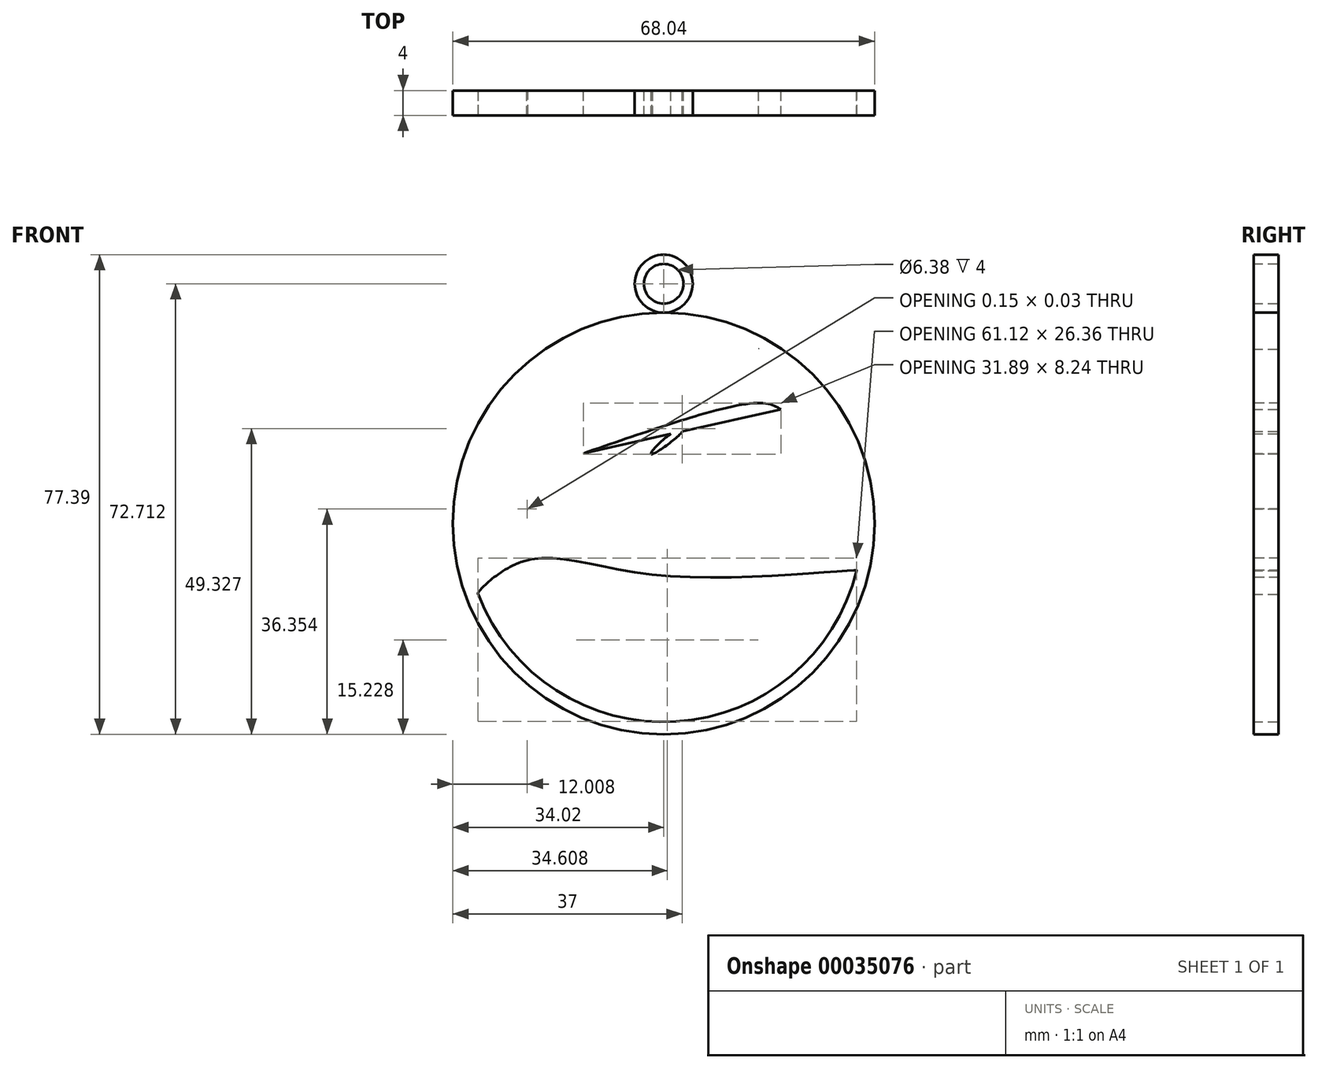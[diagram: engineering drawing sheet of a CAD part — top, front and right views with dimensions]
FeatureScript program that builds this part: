
annotation { "Feature Type Name" : "Feature", "Feature Type Description" : "" }
export const myFeature = defineFeature(function(context is Context, id is Id, definition is map)
    precondition{}
    {
        {
            var Q0;
            Q0=qCreatedBy(makeId("Front.planeOp"),FACE);
            var sketch = newSketch(context, id + "F0", { "sketchPlane" : qUnion([Q0])});
            skCircle(sketch, "E0", {"center": v(0, 0) * mm, "radius": 34.02 * mm});
            skPoint(sketch, "E1", {"position": v(0, 38.7) * mm});
            skCircle(sketch, "E2", {"center": v(0, 38.7) * mm, "radius": 4.67 * mm});
            skCircle(sketch, "E3", {"center": v(0, 38.7) * mm, "radius": 3.19 * mm});
            skCircle(sketch, "E4", {"center": v(0, 0) * mm, "radius": 32.04 * mm});
            skFitSpline(sketch, "E5", {"points": [v(-29.97, -11.33) * mm, v(-24.66, -10.38) * mm, v(22.25, -13.59) * mm, v(31.12, -7.6) * mm, v(31.14, -7.55) * mm, v(0, -8.43) * mm, v(-23.06, -6.25) * mm, v(-29.97, -11.33) * mm]});
            skFitSpline(sketch, "E6", {"points": [v(-23.06, -6.25) * mm, v(-14.23, 0) * mm, v(-29.25, 3.16) * mm, v(-29.02, 3.04) * mm, v(-18.7, 0) * mm], "startDerivative": vector(53.34, 22.76) * mm, "endDerivative": vector(45.6, -13.32) * mm});
            skFitSpline(sketch, "E7", {"points": [v(-18.7, 0) * mm, v(-19.73, -2.8) * mm, v(-23.95, -6.6) * mm, v(-23.06, -6.25) * mm], "startDerivative": vector(-0.5, -7.48) * mm, "endDerivative": vector(7.16, 3.44) * mm});
            skFitSpline(sketch, "E8", {"points": [v(-21.94, 2.33) * mm, v(-24.55, 6.83) * mm, v(-23.06, 6.94) * mm, v(-23.06, 6.83) * mm, v(-21.94, 2.33) * mm]});
            skLineSegment(sketch, "E9", {"start": v(12.5, 12.45) * mm, "end": v(12.5, -4.76) * mm});
            skLineSegment(sketch, "E10", {"start": v(-1.95, 11.19) * mm, "end": v(-1.95, -5.9) * mm});
            skLineSegment(sketch, "E11", {"start": v(-1.95, -5.9) * mm, "end": v(9.52, -6.82) * mm});
            skLineSegment(sketch, "E12", {"start": v(-1.95, 11.19) * mm, "end": v(9.52, 13.25) * mm});
            skLineSegment(sketch, "E13", {"start": v(0, -3.95) * mm, "end": v(0, 8.32) * mm});
            skFitSpline(sketch, "E14", {"points": [v(0, 8.32) * mm, v(1.37, 8.32) * mm, v(9.52, 13.25) * mm], "startDerivative": vector(4.13, -0.94) * mm, "endDerivative": vector(13.5, 9.27) * mm});
            skFitSpline(sketch, "E15", {"points": [v(0, -3.95) * mm, v(1.6, -3.95) * mm, v(9.52, -6.82) * mm], "startDerivative": vector(4.35, 0.63) * mm, "endDerivative": vector(13.49, -5.55) * mm});
            skLineSegment(sketch, "E16", {"start": v(12.5, 12.45) * mm, "end": v(9.52, 13.25) * mm});
            skLineSegment(sketch, "E17", {"start": v(9.52, 13.25) * mm, "end": v(10.13, 9.87) * mm});
            skLineSegment(sketch, "E18", {"start": v(10.13, 9.87) * mm, "end": v(10.13, -4.3) * mm});
            skLineSegment(sketch, "E19", {"start": v(10.13, -4.3) * mm, "end": v(12.5, -4.76) * mm});
            skLineSegment(sketch, "E20", {"start": v(10.13, 5.22) * mm, "end": v(2.3, 4.3) * mm});
            skLineSegment(sketch, "E21", {"start": v(10.13, 0) * mm, "end": v(2.3, -0.92) * mm});
            skFitSpline(sketch, "E22", {"points": [v(2.3, -0.92) * mm, v(3.2, -2.23) * mm, v(10.13, -0.92) * mm], "startDerivative": vector(1.65, -5.05) * mm, "endDerivative": vector(12.72, 3.98) * mm});
            skFitSpline(sketch, "E23", {"points": [v(2.3, 4.3) * mm, v(3.55, 6.14) * mm, v(10.13, 5.22) * mm], "startDerivative": vector(2.17, 6.19) * mm, "endDerivative": vector(12.58, -3.5) * mm});
            skLineSegment(sketch, "E24", {"start": v(-12.96, 11.3) * mm, "end": v(18.92, 18.41) * mm});
            skFitSpline(sketch, "E25", {"points": [v(18.92, 18.41) * mm, v(15.37, 19.45) * mm, v(-12.96, 11.3) * mm], "startDerivative": vector(-10.35, 5.9) * mm, "endDerivative": vector(-47.52, -16.56) * mm});
            skFitSpline(sketch, "E26", {"points": [v(5.73, 17.5) * mm, v(15.3, 28.14) * mm, v(15.3, 28.15) * mm], "startDerivative": vector(14.6, 16.1) * mm, "endDerivative": vector(-0.3, 0.02) * mm});
            skFitSpline(sketch, "E27", {"points": [v(15.3, 28.14) * mm, v(11, 27.02) * mm, v(5.73, 17.5) * mm], "startDerivative": vector(-11.49, -0.41) * mm, "endDerivative": vector(-7.92, -19.47) * mm});
            skFitSpline(sketch, "E28", {"points": [v(-1.27, 15.38) * mm, v(-4.02, 20.94) * mm, v(-4.25, 21.17) * mm, v(-4.93, 18.53) * mm, v(-1.27, 15.38) * mm]});
            skFitSpline(sketch, "E29", {"points": [v(-1.95, 11.19) * mm, v(1.16, 14.45) * mm, v(2.98, 14.86) * mm, v(-1.95, 11.19) * mm]});
            skSolve(sketch);
        }
        {
            var Q0;
            {var subQ0=sQuery(id+"F0.wireOp",EDGE,"E7");var subQ3=sQuery(id+"F0.wireOp",EDGE,"E6");var subQ4=makeQuery(id+"F0.imprint","INTERSECT",VERTEX,{"derivedFrom":[subQ3,subQ0]});Q0=makeQuery(id+"F0.imprint","IMPRINT",FACE,{"disambiguationData":[TD([[makeQuery(id+"F0.imprint","IMPRINT",EDGE,{"disambiguationData":[TD([[subQ4,1.0]])],"derivedFrom":subQ3}),1.0]])]});}
            var Q1;
            {var subQ0=sQuery(id+"F0.wireOp",EDGE,"E8");var subQ1=sQuery(id+"F0.wireOp",EDGE,"E6");var subQ3=makeQuery(id+"F0.imprint","INTERSECT",VERTEX,{"disambiguationData":[OD(0.0)],"derivedFrom":[subQ1,subQ0]});Q1=makeQuery(id+"F0.imprint","IMPRINT",FACE,{"disambiguationData":[TD([[makeQuery(id+"F0.imprint","IMPRINT",EDGE,{"disambiguationData":[TD([[subQ3,-1.0]])],"derivedFrom":subQ1}),-1.0]])]});}
            var Q2;
            {var subQ0=sQuery(id+"F0.wireOp",EDGE,"E5");var subQ3=sQuery(id+"F0.wireOp",EDGE,"E4");var subQ4=makeQuery(id+"F0.imprint","INTERSECT",VERTEX,{"disambiguationData":[OD(0.0)],"derivedFrom":[subQ3,subQ0]});Q2=makeQuery(id+"F0.imprint","IMPRINT",FACE,{"disambiguationData":[TD([[makeQuery(id+"F0.imprint","IMPRINT",EDGE,{"disambiguationData":[TD([[subQ4,-1.0]])],"derivedFrom":subQ3}),1.0]])]});}
            var Q3;
            {var subQ3=sQuery(id+"F0.wireOp",EDGE,"E10");Q3=makeQuery(id+"F0.imprint","IMPRINT",FACE,{"disambiguationData":[TD([[makeQuery(id+"F0.imprint","IMPRINT",EDGE,{"derivedFrom":subQ3}),1.0]])]});}
            var Q4;
            {var subQ1=sQuery(id+"F0.wireOp",EDGE,"E21");Q4=makeQuery(id+"F0.imprint","IMPRINT",FACE,{"disambiguationData":[TD([[makeQuery(id+"F0.imprint","IMPRINT",EDGE,{"derivedFrom":subQ1}),1.0]])]});}
            var Q5;
            Q5=makeQuery(id+"F0.imprint","IMPRINT",FACE,{"disambiguationData":[TD([[makeQuery(id+"F0.imprint","IMPRINT",EDGE,{"derivedFrom":sQuery(id+"F0.wireOp",EDGE,"E20")}),-1.0]])]});
            var Q6;
            Q6=makeQuery(id+"F0.imprint","IMPRINT",FACE,{"disambiguationData":[TD([[makeQuery(id+"F0.imprint","IMPRINT",EDGE,{"derivedFrom":sQuery(id+"F0.wireOp",EDGE,"E9")}),-1.0]])]});
            var Q7;
            {var subQ0=sQuery(id+"F0.wireOp",EDGE,"E25");var subQ2=sQuery(id+"F0.wireOp",EDGE,"E24");var subQ3=makeQuery(id+"F0.imprint","INTERSECT",VERTEX,{"disambiguationData":[OD(0.0)],"derivedFrom":[subQ2,subQ0]});Q7=makeQuery(id+"F0.imprint","IMPRINT",FACE,{"disambiguationData":[TD([[makeQuery(id+"F0.imprint","IMPRINT",EDGE,{"disambiguationData":[TD([[subQ3,-1.0]])],"derivedFrom":subQ2}),1.0]])]});}
            var Q8;
            {var subQ0=sQuery(id+"F0.wireOp",EDGE,"E29");var subQ1=sQuery(id+"F0.wireOp",EDGE,"E24");var subQ5=makeQuery(id+"F0.imprint","INTERSECT",VERTEX,{"disambiguationData":[OD(0.0)],"derivedFrom":[subQ1,subQ0]});Q8=makeQuery(id+"F0.imprint","IMPRINT",FACE,{"disambiguationData":[TD([[makeQuery(id+"F0.imprint","IMPRINT",EDGE,{"disambiguationData":[TD([[subQ5,-1.0]])],"derivedFrom":subQ1}),-1.0]])]});}
            var Q9;
            {var subQ0=sQuery(id+"F0.wireOp",EDGE,"E27");Q9=makeQuery(id+"F0.imprint","IMPRINT",FACE,{"disambiguationData":[TD([[makeQuery(id+"F0.imprint","IMPRINT",EDGE,{"derivedFrom":subQ0}),1.0]])]});}
            var Q10;
            Q10=makeQuery(id+"F0.imprint","IMPRINT",FACE,{"disambiguationData":[TD([[makeQuery(id+"F0.imprint","IMPRINT",EDGE,{"derivedFrom":sQuery(id+"F0.wireOp",EDGE,"E28")}),1.0]])]});
            var Q11;
            Q11=makeQuery(id+"F0.imprint","IMPRINT",FACE,{"disambiguationData":[TD([[makeQuery(id+"F0.imprint","IMPRINT",EDGE,{"derivedFrom":sQuery(id+"F0.wireOp",EDGE,"E0")}),1.0]])]});
            var Q12;
            Q12=makeQuery(id+"F0.imprint","IMPRINT",FACE,{"disambiguationData":[TD([[makeQuery(id+"F0.imprint","IMPRINT",EDGE,{"derivedFrom":sQuery(id+"F0.wireOp",EDGE,"E2")}),1.0]])]});
            extrude(context, id + "F1", {"entities" : qUnion([Q0, Q1, Q2, Q3, Q4, Q5, Q6, Q7, Q8, Q9, Q10, Q11, Q12]), "endBound" : BoundingType.SYMMETRIC, "depth" : 4 * mm});
        }
    });
